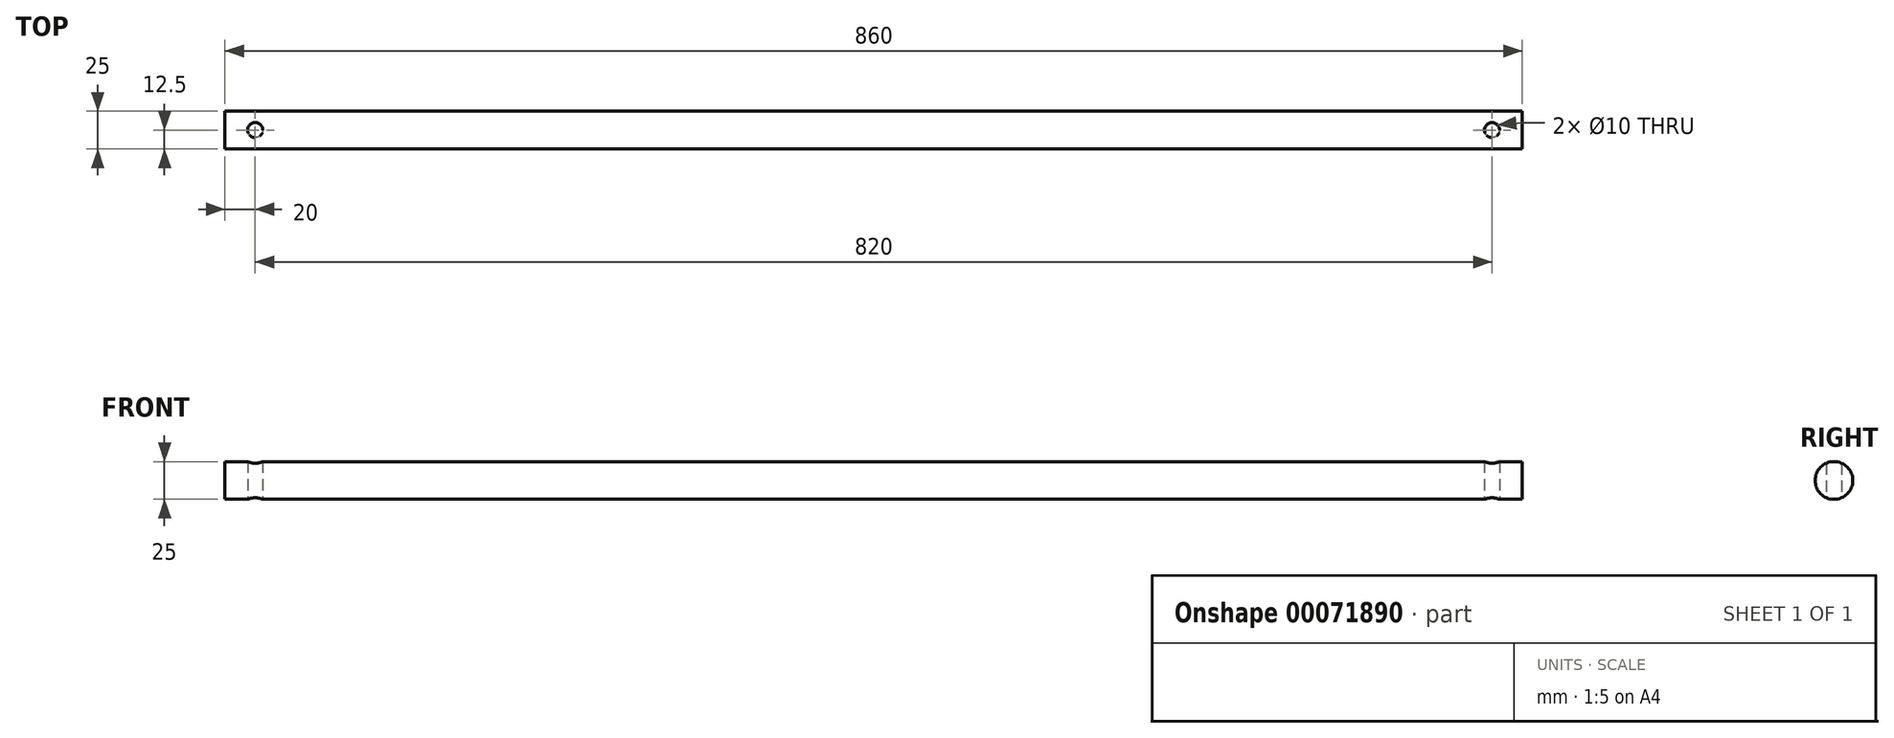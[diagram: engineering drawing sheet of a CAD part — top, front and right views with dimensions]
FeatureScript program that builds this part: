
annotation { "Feature Type Name" : "Feature", "Feature Type Description" : "" }
export const myFeature = defineFeature(function(context is Context, id is Id, definition is map)
    precondition{}
    {
        {
            var Q0;
            Q0=qCreatedBy(makeId("Right.planeOp"),FACE);
            var sketch = newSketch(context, id + "F0", { "sketchPlane" : qUnion([Q0])});
            skCircle(sketch, "E0", {"center": v(0, 0) * mm, "radius": 12.5 * mm});
            skSolve(sketch);
        }
        {
            var Q0;
            Q0 = qSketchRegion(id + "F0", true);
            extrude(context, id + "F1", {"entities" : qUnion([Q0]), "depth" : 860 * mm});
        }
        {
            var Q0;
            Q0=qCreatedBy(makeId("Top.planeOp"),FACE);
            var sketch = newSketch(context, id + "F2", { "sketchPlane" : qUnion([Q0])});
            skCircle(sketch, "E1", {"center": v(20, 0) * mm, "radius": 5 * mm});
            skCircle(sketch, "E2", {"center": v(840, 0) * mm, "radius": 5 * mm});
            skSolve(sketch);
        }
        {
            var Q0;
            Q0 = qSketchRegion(id + "F2", true);
            extrude(context, id + "F3", {"entities" : qUnion([Q0]), "operationType" : NewBodyOperationType.REMOVE, "endBound" : BoundingType.THROUGH_ALL, "depth" : 25 * mm, "hasSecondDirection" : true, "secondDirectionBound" : SecondDirectionBoundingType.THROUGH_ALL, "secondDirectionOppositeDirection" : true, "secondDirectionDepth" : 25 * mm});
        }
    });
